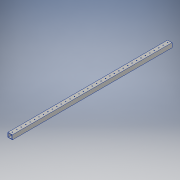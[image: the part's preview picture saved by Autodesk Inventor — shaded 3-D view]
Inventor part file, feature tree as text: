
AUTODESK INVENTOR PART (.ipt)
format: ipt  version: 2018 (Build 220112000, 112)  size: 196,608 bytes
history: native  units: in
note: dims shown in document units (in); Inventor stores cm internally (conversion verified against a paired STEP export)
features: other x5, sketch x3, hole x2, pattern_linear x2, projected_geometry x2, extrude x1
ambient origin geometry x8: Origin, YZ Plane, XZ Plane, XY Plane, X Axis, Y Axis, Z Axis, Center Point
bodies: Solid1 (feature_tree)
feature tree (15):
  other  "Table"
  other  "versatubing_1x1x40-"
  other  "versatubing_1x1x100-"
  other  "versatubing_1x2x100-"
  other  "versatubing_1x2ABS-"
  extrude  "Extrusion1"  Depth=1.0in
  hole  "Hole3"  [1 undecoded]
  hole  "Hole4"  [1 undecoded]
  pattern_linear  "Rectangular Pattern1"  Spacing1=1.0in  [1 undecoded]
  pattern_linear  "Rectangular Pattern2"  Count1=37  [1 undecoded]
  sketch  "Sketch1"  dims[d4=0.0in d5=1.0in]
  sketch  "Sketch2"  dims[d6=0.5in d7=0.5in]
  projected_geometry  "Projected Loop1"
  sketch  "Sketch3"  dims[d22=1.0in d23=0.5in d24=1.0in d39=0.161in d40=0.75in d41=0.375in d42=0.25in d43=0.5635in d44=1.0in d45=0.8108in d46=0.161in d47=0.75in d48=0.375in d49=0.25in d50=0.5635in d51=1.0in d52=0.8108in d53=14.5669in d55=1.0in d56=14.5669in d58=1.0in]
  projected_geometry  "Projected Loop2"
note: 4 required parameter values undecoded (feature->parameter linkage not recoverable at this tier; creation-order binding heuristic only, values carry confidence <= 0.55)
